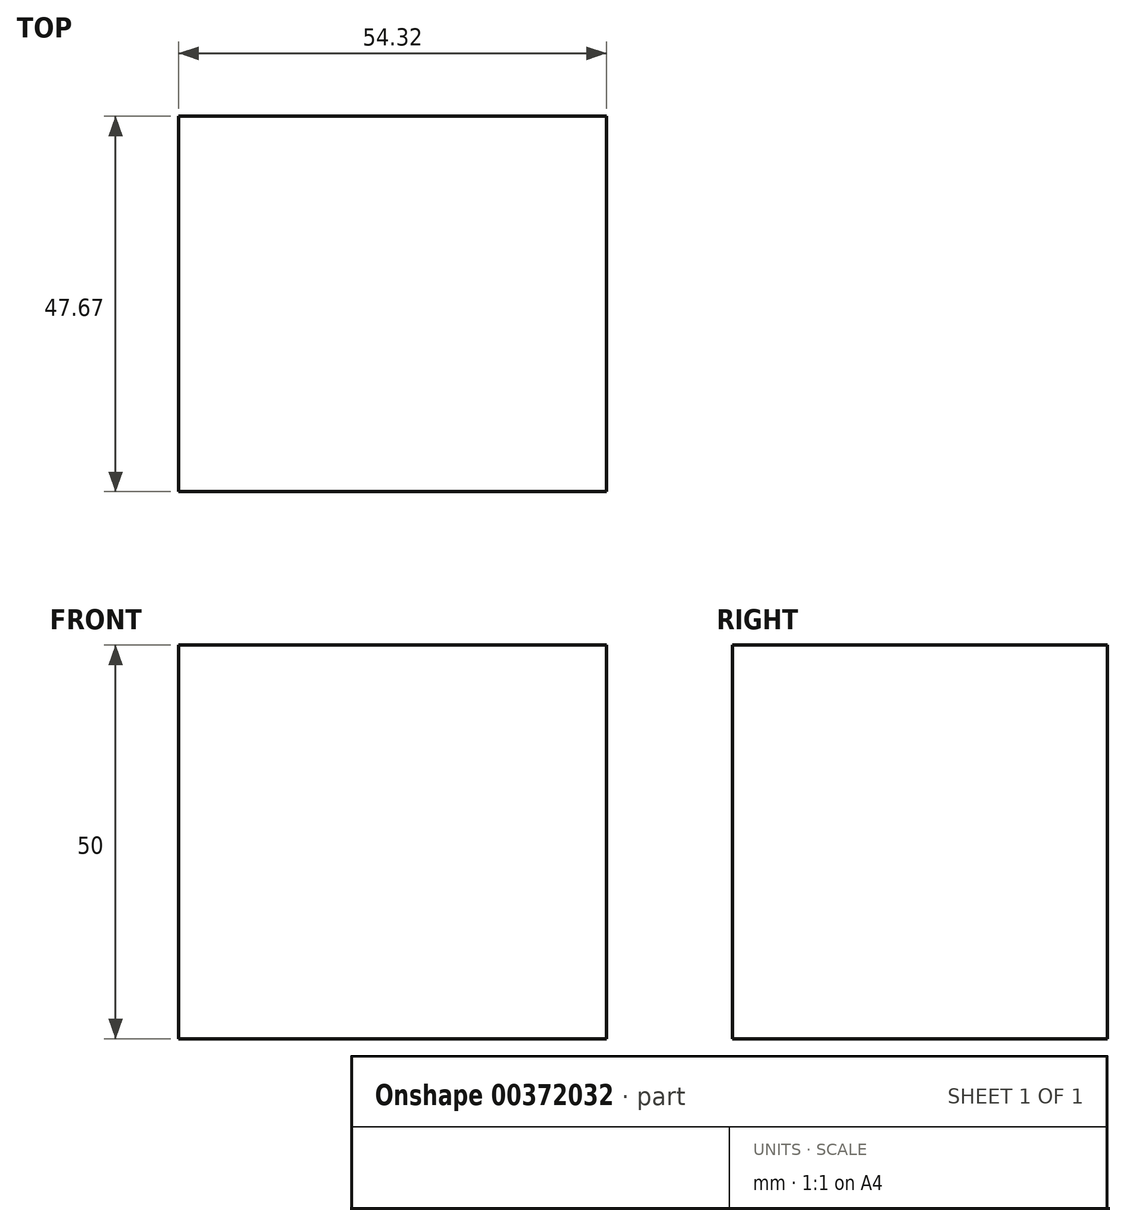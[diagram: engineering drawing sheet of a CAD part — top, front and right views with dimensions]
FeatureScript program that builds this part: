
annotation { "Feature Type Name" : "Feature", "Feature Type Description" : "" }
export const myFeature = defineFeature(function(context is Context, id is Id, definition is map)
    precondition{}
    {
        {
            var Q0;
            Q0=qCreatedBy(makeId("Top.planeOp"),FACE);
            var sketch = newSketch(context, id + "F0", { "sketchPlane" : qUnion([Q0])});
            skLineSegment(sketch, "E0.bottom", {"start": v(0, 0) * mm, "end": v(54.32, 0) * mm});
            skLineSegment(sketch, "E0.top", {"start": v(0, 47.67) * mm, "end": v(54.32, 47.67) * mm});
            skLineSegment(sketch, "E0.left", {"start": v(0, 0) * mm, "end": v(0, 47.67) * mm});
            skLineSegment(sketch, "E0.right", {"start": v(54.32, 0) * mm, "end": v(54.32, 47.67) * mm});
            skSolve(sketch);
        }
        {
            var Q0;
            Q0 = qSketchRegion(id + "F0", true);
            extrude(context, id + "F1", {"entities" : qUnion([Q0]), "depth" : 50 * mm});
        }
    });
